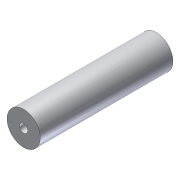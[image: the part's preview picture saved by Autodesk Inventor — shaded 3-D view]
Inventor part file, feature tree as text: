
AUTODESK INVENTOR PART (.ipt)
format: ipt  version: 2012 (Build 160160000, 160)  size: 77,312 bytes
history: native  units: in
note: dims shown in document units (in); Inventor stores cm internally (conversion verified against a paired STEP export)
features: extrude x1, sketch x1
ambient origin geometry x8: Origin, YZ Plane, XZ Plane, XY Plane, X Axis, Y Axis, Z Axis, Center Point
bodies: Solid1 (feature_tree)
feature tree (2):
  extrude  "Extrusion1"  Depth=1.5in
  sketch  "Sketch1"  dims[d0=0.375in d1=1.5in d2=6.0in d3=0.0in]
